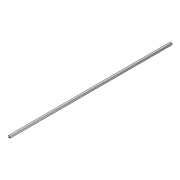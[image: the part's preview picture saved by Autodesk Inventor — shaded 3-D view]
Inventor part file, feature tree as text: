
AUTODESK INVENTOR PART (.ipt)
format: ipt  version: 2012 (Build 160160000, 160)  size: 71,680 bytes
history: native  units: in
note: dims shown in document units (in); Inventor stores cm internally (conversion verified against a paired STEP export)
features: extrude x1, sketch x1
ambient origin geometry x8: Origin, YZ Plane, XZ Plane, XY Plane, X Axis, Y Axis, Z Axis, Center Point
bodies: Solid1 (feature_tree)
feature tree (2):
  extrude  "Extrusion1"  Depth=0.75in
  sketch  "Sketch1"  dims[d0=0.75in d1=0.75in d2=0.125in d3=0.125in d4=0.125in d5=67.0in d6=0.0in]
